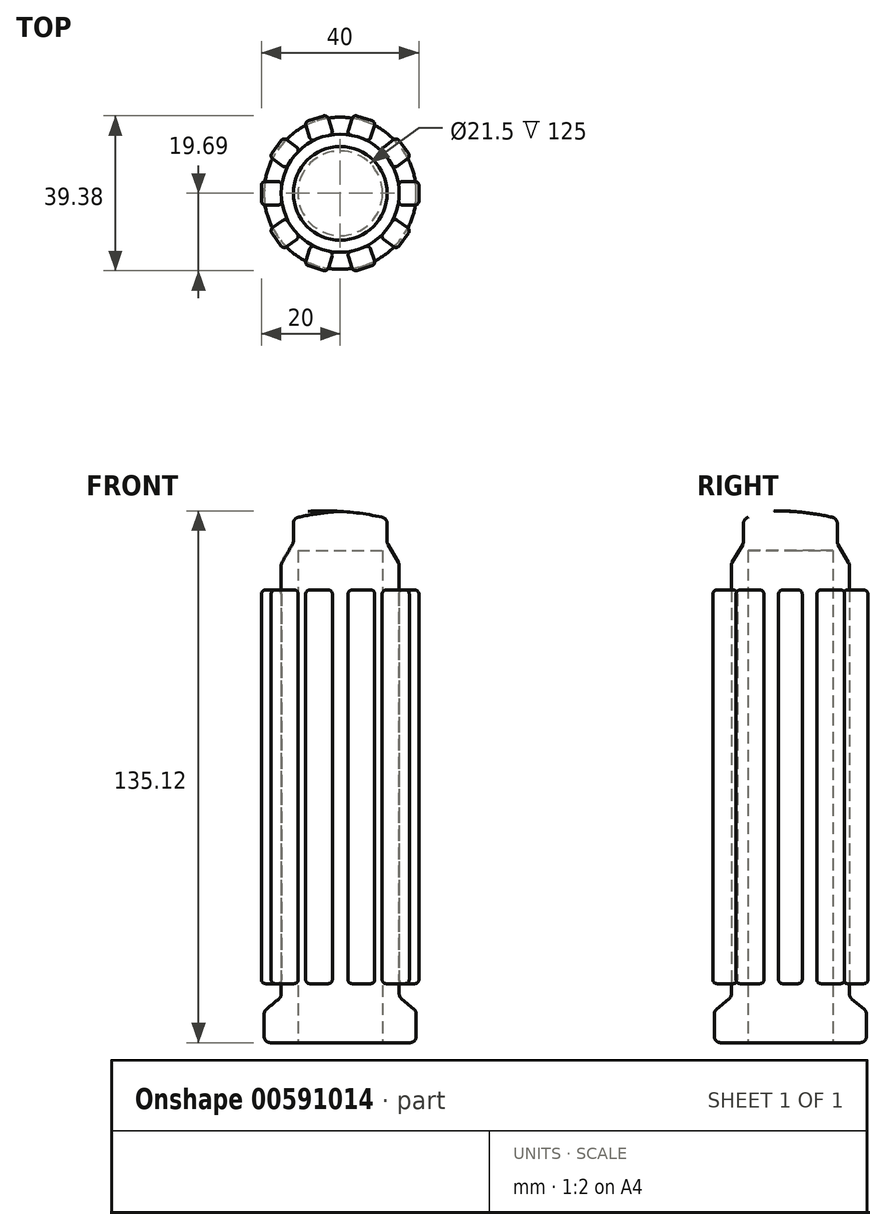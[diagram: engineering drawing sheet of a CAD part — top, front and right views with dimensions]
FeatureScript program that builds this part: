
annotation { "Feature Type Name" : "Feature", "Feature Type Description" : "" }
export const myFeature = defineFeature(function(context is Context, id is Id, definition is map)
    precondition{}
    {
        {
            var Q0;
            Q0=qCreatedBy(makeId("Front.planeOp"),FACE);
            var sketch = newSketch(context, id + "F0", { "sketchPlane" : qUnion([Q0])});
            skLineSegment(sketch, "E0", {"start": v(0, 0) * mm, "end": v(0, 125) * mm, "construction": true});
            skLineSegment(sketch, "E1", {"start": v(0, 125) * mm, "end": v(0, 135) * mm});
            skLineSegment(sketch, "E2", {"start": v(0, 125) * mm, "end": v(10.75, 125) * mm});
            skLineSegment(sketch, "E3", {"start": v(10.75, 125) * mm, "end": v(10.75, 0) * mm});
            skLineSegment(sketch, "E4", {"start": v(10.75, 0) * mm, "end": v(19.32, 0) * mm});
            skLineSegment(sketch, "E5", {"start": v(19.32, 0) * mm, "end": v(19.32, 8) * mm});
            skLineSegment(sketch, "E6", {"start": v(19.33, 8) * mm, "end": v(15, 11.63) * mm});
            skLineSegment(sketch, "E7", {"start": v(15, 11.63) * mm, "end": v(15, 121.63) * mm});
            skLineSegment(sketch, "E8", {"start": v(15, 121.63) * mm, "end": v(11.9, 127) * mm});
            skLineSegment(sketch, "E9", {"start": v(11.9, 127) * mm, "end": v(11.9, 133.21) * mm});
            skArc(sketch, "E10", {"start": v(11.9, 133.21) * mm, "mid": v(5.99, 134.37) * mm, "end": v(0, 135) * mm});
            skSolve(sketch);
        }
        {
            var Q0;
            Q0 = qSketchRegion(id + "F0", true);
            var Q1;
            Q1=sQuery(id+"F0.wireOp",EDGE,"E0");
            revolve(context, id + "F1", {"surfaceOperationType" : NewSurfaceOperationType.NEW, "entities" : qUnion([Q0]), "axis" : qUnion([Q1]), "revolveType" : RevolveType.FULL});
        }
        {
            var Q0;
            Q0=makeQuery(id+"F1.opRevolve","SWEPT_EDGE",EDGE,{"disambiguationData":[OSD([sQuery(id+"F0.wireOp",EDGE,"E9"),sQuery(id+"F0.wireOp",EDGE,"E10")])]});
            var Q1;
            Q1=makeQuery(id+"F1.opRevolve","SWEPT_EDGE",EDGE,{"disambiguationData":[OSD([sQuery(id+"F0.wireOp",EDGE,"E8"),sQuery(id+"F0.wireOp",EDGE,"E9")])]});
            var Q2;
            Q2=makeQuery(id+"F1.opRevolve","SWEPT_EDGE",EDGE,{"disambiguationData":[OSD([sQuery(id+"F0.wireOp",EDGE,"E7"),sQuery(id+"F0.wireOp",EDGE,"E8")])]});
            var Q3;
            Q3=makeQuery(id+"F1.opRevolve","SWEPT_EDGE",EDGE,{"disambiguationData":[OSD([sQuery(id+"F0.wireOp",EDGE,"E6"),sQuery(id+"F0.wireOp",EDGE,"E7")])]});
            var Q4;
            Q4=makeQuery(id+"F1.opRevolve","SWEPT_EDGE",EDGE,{"disambiguationData":[OSD([sQuery(id+"F0.wireOp",EDGE,"E5"),sQuery(id+"F0.wireOp",EDGE,"E6")])]});
            var Q5;
            Q5=makeQuery(id+"F1.opRevolve","SWEPT_EDGE",EDGE,{"disambiguationData":[OSD([sQuery(id+"F0.wireOp",EDGE,"E4"),sQuery(id+"F0.wireOp",EDGE,"E5")])]});
            fillet(context, id + "F2", {"entities" : qUnion([Q0, Q1, Q2, Q3, Q4, Q5]), "radius" : 1.6 * mm, "tangentPropagation" : true, "allowEdgeOverflow" : false});
        }
        {
            var Q0;
            Q0=qCreatedBy(makeId("Right.planeOp"),FACE);
            cPlane(context, id + "F3", {"entities" : qUnion([Q0]), "cplaneType" : CPlaneType.OFFSET, "offset" : 20 * mm, "width" : 150 * mm, "height" : 150 * mm});
        }
        {
            var Q0;
            Q0=qCreatedBy(id+"F3.planeOp",FACE);
            var sketch = newSketch(context, id + "F4", { "sketchPlane" : qUnion([Q0])});
            skLineSegment(sketch, "E11.bottom", {"start": v(-3, 15) * mm, "end": v(3, 15) * mm});
            skLineSegment(sketch, "E11.top", {"start": v(-3, 115) * mm, "end": v(3, 115) * mm});
            skLineSegment(sketch, "E11.left", {"start": v(-3, 15) * mm, "end": v(-3, 115) * mm});
            skLineSegment(sketch, "E11.right", {"start": v(3, 15) * mm, "end": v(3, 115) * mm});
            skSolve(sketch);
        }
        {
            var Q0;
            Q0 = qSketchRegion(id + "F4", true);
            var Q1;
            Q1=makeQuery(id+"F1.opRevolve","SWEPT_FACE",FACE,{"disambiguationData":[OSD([sQuery(id+"F0.wireOp",EDGE,"E7")])]});
            extrude(context, id + "F5", {"entities" : qUnion([Q0]), "endBound" : BoundingType.UP_TO_SURFACE, "oppositeDirection" : true, "depth" : 25 * mm, "endBoundEntityFace" : qUnion([Q1]), "offsetDistance" : 25 * mm});
        }
        {
            var Q0;
            Q0=makeQuery(id+"F5.opExtrude","CAP_EDGE",EDGE,{"disambiguationData":[OSD([sQuery(id+"F4.wireOp",EDGE,"E11.left")])],"isStart":true});
            var Q1;
            Q1=makeQuery(id+"F5.opExtrude","CAP_EDGE",EDGE,{"disambiguationData":[OSD([sQuery(id+"F4.wireOp",EDGE,"E11.right")])],"isStart":true});
            var Q2;
            Q2=makeQuery(id+"F5.opExtrude","CAP_EDGE",EDGE,{"disambiguationData":[OSD([sQuery(id+"F4.wireOp",EDGE,"E11.top")])],"isStart":true});
            var Q3;
            Q3=makeQuery(id+"F5.opExtrude","CAP_EDGE",EDGE,{"disambiguationData":[OSD([sQuery(id+"F4.wireOp",EDGE,"E11.bottom")])],"isStart":true});
            var Q4;
            Q4=makeQuery(id+"F5.opExtrude","SWEPT_EDGE",EDGE,{"disambiguationData":[OSD([sQuery(id+"F4.wireOp",EDGE,"E11.bottom"),sQuery(id+"F4.wireOp",EDGE,"E11.left")])]});
            var Q5;
            Q5=makeQuery(id+"F5.opExtrude","SWEPT_EDGE",EDGE,{"disambiguationData":[OSD([sQuery(id+"F4.wireOp",EDGE,"E11.bottom"),sQuery(id+"F4.wireOp",EDGE,"E11.right")])]});
            var Q6;
            Q6=makeQuery(id+"F5.opExtrude","SWEPT_EDGE",EDGE,{"disambiguationData":[OSD([sQuery(id+"F4.wireOp",EDGE,"E11.top"),sQuery(id+"F4.wireOp",EDGE,"E11.left")])]});
            var Q7;
            Q7=makeQuery(id+"F5.opExtrude","SWEPT_EDGE",EDGE,{"disambiguationData":[OSD([sQuery(id+"F4.wireOp",EDGE,"E11.top"),sQuery(id+"F4.wireOp",EDGE,"E11.right")])]});
            var Q8;
            Q8=makeQuery(id+"F5.opExtrude","CAP_EDGE",EDGE,{"disambiguationData":[OSD([sQuery(id+"F4.wireOp",EDGE,"E11.right")])],"isStart":false});
            var Q9;
            Q9=makeQuery(id+"F5.opExtrude","CAP_EDGE",EDGE,{"disambiguationData":[OSD([sQuery(id+"F4.wireOp",EDGE,"E11.top")])],"isStart":false});
            var Q10;
            Q10=makeQuery(id+"F5.opExtrude","CAP_EDGE",EDGE,{"disambiguationData":[OSD([sQuery(id+"F4.wireOp",EDGE,"E11.left")])],"isStart":false});
            var Q11;
            Q11=makeQuery(id+"F5.opExtrude","CAP_EDGE",EDGE,{"disambiguationData":[OSD([sQuery(id+"F4.wireOp",EDGE,"E11.bottom")])],"isStart":false});
            fillet(context, id + "F6", {"entities" : qUnion([Q0, Q1, Q2, Q3, Q4, Q5, Q6, Q7, Q8, Q9, Q10, Q11]), "radius" : 1 * mm, "tangentPropagation" : true, "allowEdgeOverflow" : false});
        }
        {
            var Q0;
            Q0=makeQuery(id+"F5.opExtrude","SWEPT_BODY",BODY,{"disambiguationData":[OSD([sQuery(id+"F4.wireOp",EDGE,"E11.bottom"),sQuery(id+"F4.wireOp",EDGE,"E11.top"),sQuery(id+"F4.wireOp",EDGE,"E11.left"),sQuery(id+"F4.wireOp",EDGE,"E11.right")])]});
            var Q1;
            Q1=sQuery(id+"F0.wireOp",EDGE,"E0");
            circularPattern(context, id + "F7", {"entities" : qUnion([Q0]), "axis" : qUnion([Q1]), "angle" : 360 * degree, "instanceCount" : 10, "equalSpace" : true});
        }
    });
